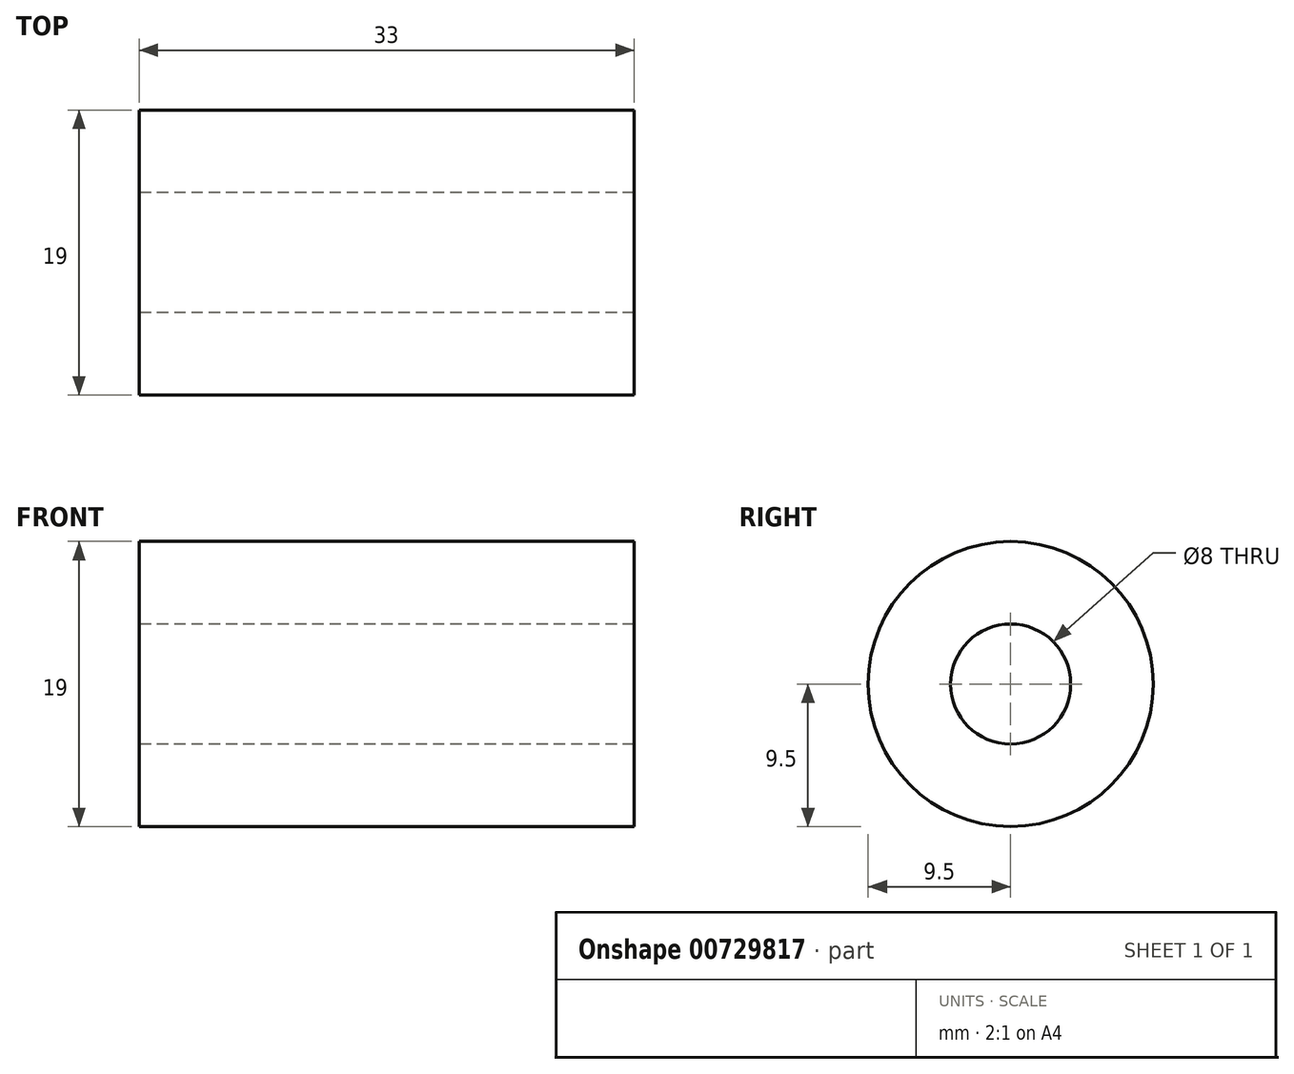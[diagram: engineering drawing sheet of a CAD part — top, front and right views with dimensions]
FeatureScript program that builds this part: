
annotation { "Feature Type Name" : "Feature", "Feature Type Description" : "" }
export const myFeature = defineFeature(function(context is Context, id is Id, definition is map)
    precondition{}
    {
        {
            var Q0;
            Q0=qCreatedBy(makeId("Right.planeOp"),FACE);
            var sketch = newSketch(context, id + "F0", { "sketchPlane" : qUnion([Q0])});
            skCircle(sketch, "E0", {"center": v(0, 0) * mm, "radius": 4 * mm});
            skCircle(sketch, "E1", {"center": v(0, 0) * mm, "radius": 9.5 * mm});
            skSolve(sketch);
        }
        {
            var Q0;
            Q0 = qSketchRegion(id + "F0", true);
            extrude(context, id + "F1", {"entities" : qUnion([Q0]), "depth" : 33 * mm, "offsetDistance" : 25 * mm});
        }
    });
